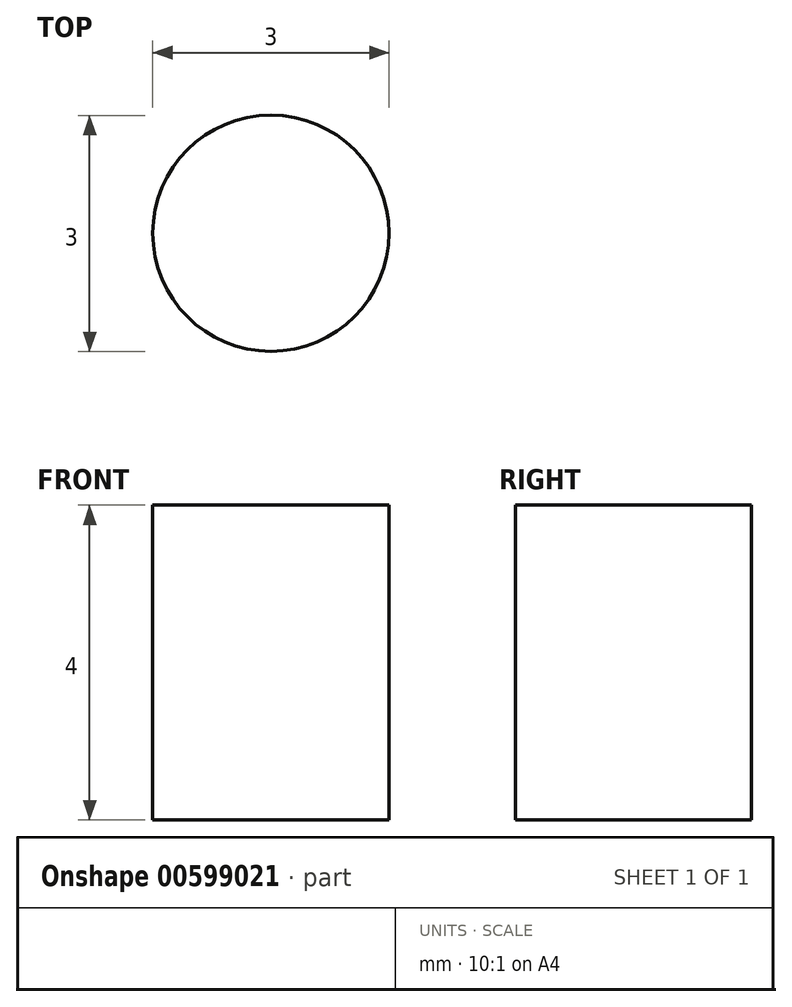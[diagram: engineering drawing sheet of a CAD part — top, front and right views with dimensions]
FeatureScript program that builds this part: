
annotation { "Feature Type Name" : "Feature", "Feature Type Description" : "" }
export const myFeature = defineFeature(function(context is Context, id is Id, definition is map)
    precondition{}
    {
        {
            var Q0;
            Q0=qCreatedBy(makeId("Top.planeOp"),FACE);
            var sketch = newSketch(context, id + "F0", { "sketchPlane" : qUnion([Q0])});
            skCircle(sketch, "E0", {"center": v(15.25, 15.25) * mm, "radius": 1.65 * mm});
            skPoint(sketch, "E1.middle", {"position": v(84.85, 84.85) * mm});
            skLineSegment(sketch, "E2.cCircle", {"start": v(56.25, 56.25) * mm, "end": v(56.25, 56.25) * mm});
            skLineSegment(sketch, "E3", {"start": v(84.85, 84.85) * mm, "end": v(0, 0) * mm, "construction": true});
            skLineSegment(sketch, "E4", {"start": v(14, 40) * mm, "end": v(11.06, 40) * mm});
            skCircle(sketch, "E5", {"center": v(84.85, 84.85) * mm, "radius": 63.5 * mm, "construction": true});
            skLineSegment(sketch, "E6", {"start": v(5.38, 24.29) * mm, "end": v(0, 24.29) * mm});
            skLineSegment(sketch, "E7", {"start": v(5.38, 24.29) * mm, "end": v(7.5, 26.4) * mm});
            skLineSegment(sketch, "E8", {"start": v(7.5, 26.4) * mm, "end": v(5.38, 28.53) * mm});
            skLineSegment(sketch, "E9", {"start": v(5.38, 28.53) * mm, "end": v(0, 28.53) * mm});
            skLineSegment(sketch, "E10", {"start": v(14, 40) * mm, "end": v(14, 0) * mm, "construction": true});
            skLineSegment(sketch, "E11.MirrorCS", {"start": v(-7.5, 26.4) * mm, "end": v(-5.38, 28.53) * mm});
            skLineSegment(sketch, "E12.MirrorCS", {"start": v(-5.38, 24.29) * mm, "end": v(-7.5, 26.4) * mm});
            skLineSegment(sketch, "E13.MirrorCS", {"start": v(-5.38, 28.53) * mm, "end": v(0, 28.53) * mm});
            skLineSegment(sketch, "E14.MirrorCS", {"start": v(-5.38, 24.29) * mm, "end": v(0, 24.29) * mm});
            skLineSegment(sketch, "E15.MirrorCS", {"start": v(20, 11.4) * mm, "end": v(17, 10) * mm});
            skLineSegment(sketch, "E16.MirrorCS", {"start": v(17, 10) * mm, "end": v(17, 0) * mm});
            skCircle(sketch, "E17", {"center": v(84.85, 84.85) * mm, "radius": 4.15 * mm});
            skLineSegment(sketch, "E18", {"start": v(20, 11.4) * mm, "end": v(78.33, 71.04) * mm});
            skLineSegment(sketch, "E19", {"start": v(14, 40) * mm, "end": v(20, 40) * mm, "construction": true});
            skLineSegment(sketch, "E20", {"start": v(20, 40) * mm, "end": v(20, 34) * mm, "construction": true});
            skLineSegment(sketch, "E21", {"start": v(20, 34) * mm, "end": v(14, 34) * mm, "construction": true});
            skCircle(sketch, "E22", {"center": v(17, 37) * mm, "radius": 1.65 * mm});
            skPoint(sketch, "E22.centerSnap0", {"position": v(20, 37) * mm});
            skPoint(sketch, "E22.centerSnap1", {"position": v(17, 40) * mm});
            skArc(sketch, "E23", {"start": v(83.25, 92.85) * mm, "mid": v(84.85, 91.25) * mm, "end": v(86.45, 92.85) * mm});
            skLineSegment(sketch, "E24.trimOffspring", {"start": v(86.45, 92.85) * mm, "end": v(86.45, 94.85) * mm});
            skLineSegment(sketch, "E25.trimOffspring", {"start": v(83.25, 92.85) * mm, "end": v(83.25, 94.35) * mm});
            skLineSegment(sketch, "E26.MirrorCS", {"start": v(83.25, 94.85) * mm, "end": v(83.25, 93.5) * mm});
            skLineSegment(sketch, "E27", {"start": v(14, 40) * mm, "end": v(20, 40) * mm});
            skLineSegment(sketch, "E28", {"start": v(20, 40) * mm, "end": v(80.19, 101.53) * mm});
            skCircle(sketch, "E29.cCircle", {"center": v(84.85, 84.85) * mm, "radius": 15 * mm, "construction": true});
            skLineSegment(sketch, "E29.0", {"start": v(68.07, 89.15) * mm, "end": v(80.19, 101.53) * mm});
            skLineSegment(sketch, "E29.1", {"start": v(80.19, 101.53) * mm, "end": v(96.96, 97.24) * mm});
            skLineSegment(sketch, "E29.2", {"start": v(96.96, 97.24) * mm, "end": v(101.63, 80.56) * mm});
            skLineSegment(sketch, "E29.3", {"start": v(101.63, 80.56) * mm, "end": v(89.52, 68.17) * mm});
            skLineSegment(sketch, "E29.4", {"start": v(89.52, 68.17) * mm, "end": v(72.74, 72.47) * mm});
            skLineSegment(sketch, "E29.5", {"start": v(72.74, 72.47) * mm, "end": v(68.07, 89.15) * mm});
            skPoint(sketch, "E29.0.midPoint", {"position": v(74.13, 95.34) * mm});
            skLineSegment(sketch, "E30", {"start": v(20, 11.4) * mm, "end": v(20, 34) * mm, "construction": true});
            skLineSegment(sketch, "E31", {"start": v(0, 37.6) * mm, "end": v(0, 28.53) * mm});
            skLineSegment(sketch, "E32", {"start": v(0, 24.29) * mm, "end": v(0, 0) * mm});
            skLineSegment(sketch, "E33", {"start": v(17, 0) * mm, "end": v(0, 0) * mm});
            skLineSegment(sketch, "E34", {"start": v(0, 37.6) * mm, "end": v(9, 37.6) * mm});
            skLineSegment(sketch, "E35", {"start": v(9, 37.6) * mm, "end": v(11.06, 40) * mm});
            skLineSegment(sketch, "E36", {"start": v(77.58, 84.85) * mm, "end": v(91.14, 84.85) * mm, "construction": true});
            skLineSegment(sketch, "E37", {"start": v(84.85, 90.4) * mm, "end": v(84.85, 78.23) * mm, "construction": true});
            skLineSegment(sketch, "E38", {"start": v(84.85, 92.85) * mm, "end": v(84.85, 94.85) * mm, "construction": true});
            skArc(sketch, "E39", {"start": v(86.45, 94.85) * mm, "mid": v(84.85, 96.45) * mm, "end": v(83.25, 94.85) * mm});
            skArc(sketch, "E40.MirrorCS", {"start": v(86.45, 92.85) * mm, "mid": v(84.85, 91.25) * mm, "end": v(83.25, 92.85) * mm});
            skLineSegment(sketch, "E41.MirrorCS", {"start": v(86.45, 92.85) * mm, "end": v(86.45, 94.35) * mm});
            skLineSegment(sketch, "E42.MirrorCS", {"start": v(83.25, 92.85) * mm, "end": v(83.25, 94.85) * mm});
            skLineSegment(sketch, "E43.MirrorCS", {"start": v(86.45, 94.85) * mm, "end": v(86.45, 93.5) * mm});
            skArc(sketch, "E44.MirrorCS", {"start": v(83.25, 94.85) * mm, "mid": v(84.85, 96.45) * mm, "end": v(86.45, 94.85) * mm});
            skLineSegment(sketch, "E45.MirrorCS", {"start": v(83.25, 94.85) * mm, "end": v(83.25, 95.2) * mm});
            skArc(sketch, "E46.MirrorCS", {"start": v(86.45, 76.85) * mm, "mid": v(84.85, 78.45) * mm, "end": v(83.25, 76.85) * mm});
            skLineSegment(sketch, "E47.MirrorCS", {"start": v(86.45, 76.85) * mm, "end": v(86.45, 75.35) * mm});
            skLineSegment(sketch, "E48.MirrorCS", {"start": v(86.45, 74.85) * mm, "end": v(86.45, 76.2) * mm});
            skArc(sketch, "E49.MirrorCS", {"start": v(83.25, 74.85) * mm, "mid": v(84.85, 73.25) * mm, "end": v(86.45, 74.85) * mm});
            skLineSegment(sketch, "E50.MirrorCS", {"start": v(83.25, 74.85) * mm, "end": v(83.25, 76.2) * mm});
            skLineSegment(sketch, "E51.MirrorCS", {"start": v(83.25, 76.85) * mm, "end": v(83.25, 74.85) * mm});
            skLineSegment(sketch, "E52", {"start": v(84.85, 84.85) * mm, "end": v(76.55, 93.16) * mm, "construction": true});
            skArc(sketch, "E53.MirrorCS", {"start": v(76.85, 83.25) * mm, "mid": v(78.45, 84.85) * mm, "end": v(76.85, 86.45) * mm});
            skLineSegment(sketch, "E54.MirrorCS", {"start": v(76.85, 83.25) * mm, "end": v(75.35, 83.25) * mm});
            skLineSegment(sketch, "E55.MirrorCS", {"start": v(74.85, 83.25) * mm, "end": v(76.2, 83.25) * mm});
            skArc(sketch, "E56.MirrorCS", {"start": v(74.85, 86.45) * mm, "mid": v(73.25, 84.85) * mm, "end": v(74.85, 83.25) * mm});
            skLineSegment(sketch, "E57.MirrorCS", {"start": v(74.85, 86.45) * mm, "end": v(76.2, 86.45) * mm});
            skLineSegment(sketch, "E58.MirrorCS", {"start": v(76.85, 86.45) * mm, "end": v(74.85, 86.45) * mm});
            skArc(sketch, "E59.MirrorCS", {"start": v(92.85, 83.25) * mm, "mid": v(91.25, 84.85) * mm, "end": v(92.85, 86.45) * mm});
            skLineSegment(sketch, "E60.MirrorCS", {"start": v(92.85, 86.45) * mm, "end": v(94.85, 86.45) * mm});
            skLineSegment(sketch, "E61.MirrorCS", {"start": v(94.85, 86.45) * mm, "end": v(93.5, 86.45) * mm});
            skArc(sketch, "E62.MirrorCS", {"start": v(94.85, 86.45) * mm, "mid": v(96.45, 84.85) * mm, "end": v(94.85, 83.25) * mm});
            skLineSegment(sketch, "E63.MirrorCS", {"start": v(94.85, 83.25) * mm, "end": v(93.5, 83.25) * mm});
            skLineSegment(sketch, "E64.MirrorCS", {"start": v(92.85, 83.25) * mm, "end": v(94.35, 83.25) * mm});
            skCircle(sketch, "E65.MirrorC", {"center": v(84.85, -84.85) * mm, "radius": 63.5 * mm, "construction": true});
            skPoint(sketch, "E66.orphan", {"position": v(74.5, 86.45) * mm});
            skPoint(sketch, "E67.orphan", {"position": v(95.2, 86.45) * mm});
            skPoint(sketch, "E68.orphan", {"position": v(83.25, 74.5) * mm});
            skPoint(sketch, "E69.start.orphan", {"position": v(86.45, 95.2) * mm});
            skSolve(sketch);
        }
        {
            var Q0;
            Q0=makeQuery(id+"F0.imprint","IMPRINT",FACE,{"disambiguationData":[TD([[makeQuery(id+"F0.imprint","IMPRINT",EDGE,{"derivedFrom":sQuery(id+"F0.wireOp",EDGE,"E0")}),-1.0]])]});
            var Q1;
            Q1=makeQuery(id+"F0.imprint","IMPRINT",FACE,{"disambiguationData":[TD([[makeQuery(id+"F0.imprint","IMPRINT",EDGE,{"derivedFrom":sQuery(id+"F0.wireOp",EDGE,"a8402e06-ee66-4db1-b534-accf88d6755370.MirrorCS")}),1.0]])]});
            var Q2;
            Q2=makeQuery(id+"F0.imprint","IMPRINT",FACE,{"disambiguationData":[TD([[makeQuery(id+"F0.imprint","IMPRINT",EDGE,{"derivedFrom":sQuery(id+"F0.wireOp",EDGE,"E17")}),-1.0]])]});
            extrude(context, id + "F1", {"entities" : qUnion([Q0, Q1, Q2]), "depth" : 4 * mm, "offsetDistance" : 25 * mm});
        }
        {
            var Q0;
            Q0=makeQuery(id+"F1.opExtrude","SWEPT_EDGE",EDGE,{"disambiguationData":[OSD([sQuery(id+"F0.wireOp",EDGE,"jGvzkioU-qR6A-EtLG-xQrp-rLiX74bcyy6I"),sQuery(id+"F0.wireOp",EDGE,"c73e3937-3783-43b0-b012-681b517a04ab3.MirrorCS")])]});
            var Q1;
            Q1=makeQuery(id+"F1.opExtrude","SWEPT_EDGE",EDGE,{"disambiguationData":[OSD([sQuery(id+"F0.wireOp",EDGE,"c73e3937-3783-43b0-b012-681b517a04ab3.MirrorCS"),sQuery(id+"F0.wireOp",EDGE,"c73e3937-3783-43b0-b012-681b517a04ab4.MirrorCS")])]});
            var Q2;
            Q2=makeQuery(id+"F1.opExtrude","SWEPT_EDGE",EDGE,{"disambiguationData":[OSD([sQuery(id+"F0.wireOp",EDGE,"c73e3937-3783-43b0-b012-681b517a04ab2.MirrorCS"),sQuery(id+"F0.wireOp",EDGE,"c73e3937-3783-43b0-b012-681b517a04ab4.MirrorCS")])]});
            var Q3;
            Q3=makeQuery(id+"F1.opExtrude","SWEPT_EDGE",EDGE,{"disambiguationData":[OSD([sQuery(id+"F0.wireOp",EDGE,"c73e3937-3783-43b0-b012-681b517a04ab1.MirrorCS"),sQuery(id+"F0.wireOp",EDGE,"c73e3937-3783-43b0-b012-681b517a04ab2.MirrorCS")])]});
            var Q4;
            Q4=makeQuery(id+"F1.opExtrude","SWEPT_EDGE",EDGE,{"disambiguationData":[OSD([sQuery(id+"F0.wireOp",EDGE,"c73e3937-3783-43b0-b012-681b517a04ab0.MirrorCS"),sQuery(id+"F0.wireOp",EDGE,"c73e3937-3783-43b0-b012-681b517a04ab1.MirrorCS")])]});
            var Q5;
            {var subQ0=sQuery(id+"F0.wireOp",EDGE,"E18");Q5=qUnion([makeQuery(id+"F1.opExtrude","SWEPT_EDGE",EDGE,{"disambiguationData":[OSD([sQuery(id+"F0.wireOp",EDGE,"E15.MirrorCS"),subQ0])]}),makeQuery(id+"F1.opExtrude","SWEPT_EDGE",EDGE,{"disambiguationData":[OSD([subQ0,sQuery(id+"F0.wireOp",EDGE,"E29.4")])]})]);}
            var Q6;
            {var subQ0=sQuery(id+"F0.wireOp",EDGE,"E18");Q6=qUnion([makeQuery(id+"F1.opExtrude","SWEPT_EDGE",EDGE,{"disambiguationData":[OSD([sQuery(id+"F0.wireOp",EDGE,"E15.MirrorCS"),subQ0])]}),makeQuery(id+"F1.opExtrude","SWEPT_EDGE",EDGE,{"disambiguationData":[OSD([subQ0,sQuery(id+"F0.wireOp",EDGE,"E29.4")])]})]);}
            var Q7;
            {var subQ0=sQuery(id+"F0.wireOp",EDGE,"E15.MirrorCS");Q7=qUnion([makeQuery(id+"F1.opExtrude","SWEPT_EDGE",EDGE,{"disambiguationData":[OSD([subQ0,sQuery(id+"F0.wireOp",EDGE,"E18")])]}),makeQuery(id+"F1.opExtrude","SWEPT_EDGE",EDGE,{"disambiguationData":[OSD([subQ0,sQuery(id+"F0.wireOp",EDGE,"E16.MirrorCS")])]})]);}
            var Q8;
            Q8=makeQuery(id+"F1.opExtrude","SWEPT_EDGE",EDGE,{"disambiguationData":[OSD([sQuery(id+"F0.wireOp",EDGE,"E15.MirrorCS"),sQuery(id+"F0.wireOp",EDGE,"E16.MirrorCS")])]});
            var Q9;
            Q9=makeQuery(id+"F1.opExtrude","SWEPT_EDGE",EDGE,{"disambiguationData":[OSD([sQuery(id+"F0.wireOp",EDGE,"ATg7OfvZ-YIOK-q6A6-GKlu-KA3SPvuErL9v"),sQuery(id+"F0.wireOp",EDGE,"gxQ5UFMt-oJty-NrjN-UH2Y-Adpejihou7FO")])]});
            var Q10;
            Q10=makeQuery(id+"F1.opExtrude","SWEPT_EDGE",EDGE,{"disambiguationData":[OSD([sQuery(id+"F0.wireOp",EDGE,"d21186f0-3676-4457-b274-e7f54dffb324103.MirrorCS"),sQuery(id+"F0.wireOp",EDGE,"ATg7OfvZ-YIOK-q6A6-GKlu-KA3SPvuErL9v")])]});
            var Q11;
            Q11=makeQuery(id+"F1.opExtrude","SWEPT_EDGE",EDGE,{"disambiguationData":[OSD([sQuery(id+"F0.wireOp",EDGE,"d21186f0-3676-4457-b274-e7f54dffb324103.MirrorCS"),sQuery(id+"F0.wireOp",EDGE,"6f5b9e03-edb7-4fd9-bd29-0bbe677f39fa0.MirrorCS")])]});
            var Q12;
            Q12=makeQuery(id+"F1.opExtrude","SWEPT_EDGE",EDGE,{"disambiguationData":[OSD([sQuery(id+"F0.wireOp",EDGE,"4ac17b15-1a57-428c-943a-6c9f986613ac.2"),sQuery(id+"F0.wireOp",EDGE,"6f5b9e03-edb7-4fd9-bd29-0bbe677f39fa0.MirrorCS")])]});
            var Q13;
            Q13=makeQuery(id+"F1.opExtrude","SWEPT_EDGE",EDGE,{"disambiguationData":[OSD([sQuery(id+"F0.wireOp",EDGE,"4ac17b15-1a57-428c-943a-6c9f986613ac.2"),sQuery(id+"F0.wireOp",EDGE,"4ac17b15-1a57-428c-943a-6c9f986613ac.3")])]});
            var Q14;
            Q14=makeQuery(id+"F1.opExtrude","SWEPT_EDGE",EDGE,{"disambiguationData":[OSD([sQuery(id+"F0.wireOp",EDGE,"4ac17b15-1a57-428c-943a-6c9f986613ac.3"),sQuery(id+"F0.wireOp",EDGE,"4ac17b15-1a57-428c-943a-6c9f986613ac.4")])]});
            var Q15;
            Q15=makeQuery(id+"F1.opExtrude","SWEPT_EDGE",EDGE,{"disambiguationData":[OSD([sQuery(id+"F0.wireOp",EDGE,"4ac17b15-1a57-428c-943a-6c9f986613ac.4"),sQuery(id+"F0.wireOp",EDGE,"4ac17b15-1a57-428c-943a-6c9f986613ac.5")])]});
            var Q16;
            Q16=makeQuery(id+"F1.opExtrude","SWEPT_EDGE",EDGE,{"disambiguationData":[OSD([sQuery(id+"F0.wireOp",EDGE,"4ac17b15-1a57-428c-943a-6c9f986613ac.0"),sQuery(id+"F0.wireOp",EDGE,"4ac17b15-1a57-428c-943a-6c9f986613ac.5")])]});
            var Q17;
            Q17=makeQuery(id+"F1.opExtrude","SWEPT_EDGE",EDGE,{"disambiguationData":[OSD([sQuery(id+"F0.wireOp",EDGE,"d21186f0-3676-4457-b274-e7f54dffb32479.MirrorCS"),sQuery(id+"F0.wireOp",EDGE,"4ac17b15-1a57-428c-943a-6c9f986613ac.0")])]});
            var Q18;
            Q18=makeQuery(id+"F1.opExtrude","SWEPT_EDGE",EDGE,{"disambiguationData":[OSD([sQuery(id+"F0.wireOp",EDGE,"d21186f0-3676-4457-b274-e7f54dffb32468.MirrorCS"),sQuery(id+"F0.wireOp",EDGE,"d21186f0-3676-4457-b274-e7f54dffb32479.MirrorCS")])]});
            var Q19;
            Q19=makeQuery(id+"F1.opExtrude","SWEPT_EDGE",EDGE,{"disambiguationData":[OSD([sQuery(id+"F0.wireOp",EDGE,"d21186f0-3676-4457-b274-e7f54dffb32481.MirrorCS"),sQuery(id+"F0.wireOp",EDGE,"d21186f0-3676-4457-b274-e7f54dffb324119.MirrorCS")])]});
            var Q20;
            Q20=makeQuery(id+"F1.opExtrude","SWEPT_EDGE",EDGE,{"disambiguationData":[OSD([sQuery(id+"F0.wireOp",EDGE,"d21186f0-3676-4457-b274-e7f54dffb324119.MirrorCS"),sQuery(id+"F0.wireOp",EDGE,"76a94fc9-4153-4bcc-bea7-408b991e1d1c3.MirrorCS")])]});
            var Q21;
            Q21=makeQuery(id+"F1.opExtrude","SWEPT_EDGE",EDGE,{"disambiguationData":[OSD([sQuery(id+"F0.wireOp",EDGE,"76a94fc9-4153-4bcc-bea7-408b991e1d1c3.MirrorCS"),sQuery(id+"F0.wireOp",EDGE,"76a94fc9-4153-4bcc-bea7-408b991e1d1c4.MirrorCS")])]});
            var Q22;
            Q22=makeQuery(id+"F1.opExtrude","SWEPT_EDGE",EDGE,{"disambiguationData":[OSD([sQuery(id+"F0.wireOp",EDGE,"76a94fc9-4153-4bcc-bea7-408b991e1d1c2.MirrorCS"),sQuery(id+"F0.wireOp",EDGE,"76a94fc9-4153-4bcc-bea7-408b991e1d1c4.MirrorCS")])]});
            var Q23;
            Q23=makeQuery(id+"F1.opExtrude","SWEPT_EDGE",EDGE,{"disambiguationData":[OSD([sQuery(id+"F0.wireOp",EDGE,"76a94fc9-4153-4bcc-bea7-408b991e1d1c1.MirrorCS"),sQuery(id+"F0.wireOp",EDGE,"76a94fc9-4153-4bcc-bea7-408b991e1d1c2.MirrorCS")])]});
            var Q24;
            Q24=makeQuery(id+"F1.opExtrude","SWEPT_EDGE",EDGE,{"disambiguationData":[OSD([sQuery(id+"F0.wireOp",EDGE,"76a94fc9-4153-4bcc-bea7-408b991e1d1c0.MirrorCS"),sQuery(id+"F0.wireOp",EDGE,"76a94fc9-4153-4bcc-bea7-408b991e1d1c1.MirrorCS")])]});
            var Q25;
            Q25=makeQuery(id+"F1.opExtrude","SWEPT_EDGE",EDGE,{"disambiguationData":[OSD([sQuery(id+"F0.wireOp",EDGE,"76a94fc9-4153-4bcc-bea7-408b991e1d1c0.MirrorCS"),sQuery(id+"F0.wireOp",EDGE,"6d48d0eb-1f29-4900-b3be-e3536e2e83870.MirrorCS")])]});
            var Q26;
            Q26=makeQuery(id+"F1.opExtrude","SWEPT_EDGE",EDGE,{"disambiguationData":[OSD([sQuery(id+"F0.wireOp",EDGE,"5b215c89-2612-4b35-8ec4-2e2aefe904ed2.MirrorCS"),sQuery(id+"F0.wireOp",EDGE,"6d48d0eb-1f29-4900-b3be-e3536e2e83870.MirrorCS")])]});
            var Q27;
            Q27=makeQuery(id+"F1.opExtrude","SWEPT_EDGE",EDGE,{"disambiguationData":[OSD([sQuery(id+"F0.wireOp",EDGE,"5b215c89-2612-4b35-8ec4-2e2aefe904ed2.MirrorCS"),sQuery(id+"F0.wireOp",EDGE,"5b215c89-2612-4b35-8ec4-2e2aefe904ed3.MirrorCS")])]});
            var Q28;
            Q28=makeQuery(id+"F1.opExtrude","SWEPT_EDGE",EDGE,{"disambiguationData":[OSD([sQuery(id+"F0.wireOp",EDGE,"5b215c89-2612-4b35-8ec4-2e2aefe904ed3.MirrorCS"),sQuery(id+"F0.wireOp",EDGE,"5b215c89-2612-4b35-8ec4-2e2aefe904ed4.MirrorCS")])]});
            var Q29;
            Q29=makeQuery(id+"F1.opExtrude","SWEPT_EDGE",EDGE,{"disambiguationData":[OSD([sQuery(id+"F0.wireOp",EDGE,"5b215c89-2612-4b35-8ec4-2e2aefe904ed1.MirrorCS"),sQuery(id+"F0.wireOp",EDGE,"5b215c89-2612-4b35-8ec4-2e2aefe904ed5.MirrorCS")])]});
            var Q30;
            Q30=makeQuery(id+"F1.opExtrude","SWEPT_EDGE",EDGE,{"disambiguationData":[OSD([sQuery(id+"F0.wireOp",EDGE,"5b215c89-2612-4b35-8ec4-2e2aefe904ed0.MirrorCS"),sQuery(id+"F0.wireOp",EDGE,"5b215c89-2612-4b35-8ec4-2e2aefe904ed5.MirrorCS")])]});
            var Q31;
            Q31=makeQuery(id+"F1.opExtrude","SWEPT_EDGE",EDGE,{"disambiguationData":[OSD([sQuery(id+"F0.wireOp",EDGE,"5b215c89-2612-4b35-8ec4-2e2aefe904ed0.MirrorCS"),sQuery(id+"F0.wireOp",EDGE,"7c8dc105-e33c-482c-8640-72da622ad4630.MirrorCS")])]});
            var Q32;
            Q32=makeQuery(id+"F1.opExtrude","SWEPT_EDGE",EDGE,{"disambiguationData":[OSD([sQuery(id+"F0.wireOp",EDGE,"7e529d84-9969-4e5d-990a-ac009d21d78a0.MirrorCS"),sQuery(id+"F0.wireOp",EDGE,"7c8dc105-e33c-482c-8640-72da622ad4630.MirrorCS")])]});
            var Q33;
            Q33=makeQuery(id+"F1.opExtrude","SWEPT_EDGE",EDGE,{"disambiguationData":[OSD([sQuery(id+"F0.wireOp",EDGE,"7e529d84-9969-4e5d-990a-ac009d21d78a0.MirrorCS"),sQuery(id+"F0.wireOp",EDGE,"7e529d84-9969-4e5d-990a-ac009d21d78a1.MirrorCS")])]});
            var Q34;
            Q34=makeQuery(id+"F1.opExtrude","SWEPT_EDGE",EDGE,{"disambiguationData":[OSD([sQuery(id+"F0.wireOp",EDGE,"7e529d84-9969-4e5d-990a-ac009d21d78a1.MirrorCS"),sQuery(id+"F0.wireOp",EDGE,"7e529d84-9969-4e5d-990a-ac009d21d78a2.MirrorCS")])]});
            var Q35;
            Q35=makeQuery(id+"F1.opExtrude","SWEPT_EDGE",EDGE,{"disambiguationData":[OSD([sQuery(id+"F0.wireOp",EDGE,"7e529d84-9969-4e5d-990a-ac009d21d78a2.MirrorCS"),sQuery(id+"F0.wireOp",EDGE,"7e529d84-9969-4e5d-990a-ac009d21d78a4.MirrorCS")])]});
            var Q36;
            Q36=makeQuery(id+"F1.opExtrude","SWEPT_EDGE",EDGE,{"disambiguationData":[OSD([sQuery(id+"F0.wireOp",EDGE,"7e529d84-9969-4e5d-990a-ac009d21d78a3.MirrorCS"),sQuery(id+"F0.wireOp",EDGE,"7e529d84-9969-4e5d-990a-ac009d21d78a4.MirrorCS")])]});
            var Q37;
            Q37=makeQuery(id+"F1.opExtrude","SWEPT_EDGE",EDGE,{"disambiguationData":[OSD([sQuery(id+"F0.wireOp",EDGE,"2c355935-e90a-4b73-921b-e13c2be87c5e59.MirrorCS"),sQuery(id+"F0.wireOp",EDGE,"7e529d84-9969-4e5d-990a-ac009d21d78a3.MirrorCS")])]});
            var Q38;
            Q38=makeQuery(id+"F1.opExtrude","SWEPT_EDGE",EDGE,{"disambiguationData":[OSD([sQuery(id+"F0.wireOp",EDGE,"2c355935-e90a-4b73-921b-e13c2be87c5e50.MirrorCS"),sQuery(id+"F0.wireOp",EDGE,"2c355935-e90a-4b73-921b-e13c2be87c5e59.MirrorCS")])]});
            var Q39;
            Q39=makeQuery(id+"F1.opExtrude","SWEPT_EDGE",EDGE,{"disambiguationData":[OSD([sQuery(id+"F0.wireOp",EDGE,"E29.3"),sQuery(id+"F0.wireOp",EDGE,"E29.4")])]});
            var Q40;
            Q40=makeQuery(id+"F1.opExtrude","SWEPT_EDGE",EDGE,{"disambiguationData":[OSD([sQuery(id+"F0.wireOp",EDGE,"E29.2"),sQuery(id+"F0.wireOp",EDGE,"E29.3")])]});
            var Q41;
            Q41=makeQuery(id+"F1.opExtrude","SWEPT_EDGE",EDGE,{"disambiguationData":[OSD([sQuery(id+"F0.wireOp",EDGE,"E29.1"),sQuery(id+"F0.wireOp",EDGE,"E29.2")])]});
            var Q42;
            Q42=makeQuery(id+"F1.opExtrude","SWEPT_EDGE",EDGE,{"disambiguationData":[OSD([sQuery(id+"F0.wireOp",EDGE,"E28"),sQuery(id+"F0.wireOp",EDGE,"E29.1")])]});
            var Q43;
            Q43=makeQuery(id+"F1.opExtrude","SWEPT_EDGE",EDGE,{"disambiguationData":[OSD([sQuery(id+"F0.wireOp",EDGE,"E27"),sQuery(id+"F0.wireOp",EDGE,"E28")])]});
            var Q44;
            Q44=makeQuery(id+"F1.opExtrude","SWEPT_EDGE",EDGE,{"disambiguationData":[OSD([sQuery(id+"F0.wireOp",EDGE,"E4"),sQuery(id+"F0.wireOp",EDGE,"E35")])]});
            var Q45;
            Q45=makeQuery(id+"F1.opExtrude","SWEPT_EDGE",EDGE,{"disambiguationData":[OSD([sQuery(id+"F0.wireOp",EDGE,"E34"),sQuery(id+"F0.wireOp",EDGE,"E35")])]});
            fillet(context, id + "F2", {"entities" : qUnion([Q0, Q1, Q2, Q3, Q4, Q5, Q6, Q7, Q8, Q9, Q10, Q11, Q12, Q13, Q14, Q15, Q16, Q17, Q18, Q19, Q20, Q21, Q22, Q23, Q24, Q25, Q26, Q27, Q28, Q29, Q30, Q31, Q32, Q33, Q34, Q35, Q36, Q37, Q38, Q39, Q40, Q41, Q42, Q43, Q44, Q45]), "radius" : 3 * mm, "tangentPropagation" : true, "allowEdgeOverflow" : false});
        }
        {
            var Q0;
            Q0=makeQuery(id+"F1.opExtrude","SWEPT_BODY",BODY,{"disambiguationData":[OSD([sQuery(id+"F0.wireOp",EDGE,"E0"),sQuery(id+"F0.wireOp",EDGE,"E4"),sQuery(id+"F0.wireOp",EDGE,"E6"),sQuery(id+"F0.wireOp",EDGE,"E7"),sQuery(id+"F0.wireOp",EDGE,"E8"),sQuery(id+"F0.wireOp",EDGE,"E9"),sQuery(id+"F0.wireOp",EDGE,"E15.MirrorCS"),sQuery(id+"F0.wireOp",EDGE,"E16.MirrorCS"),sQuery(id+"F0.wireOp",EDGE,"E17"),sQuery(id+"F0.wireOp",EDGE,"E18"),sQuery(id+"F0.wireOp",EDGE,"E22"),sQuery(id+"F0.wireOp",EDGE,"E23"),sQuery(id+"F0.wireOp",EDGE,"E24.trimOffspring"),sQuery(id+"F0.wireOp",EDGE,"E25.trimOffspring"),sQuery(id+"F0.wireOp",EDGE,"E26.MirrorCS"),sQuery(id+"F0.wireOp",EDGE,"E27"),sQuery(id+"F0.wireOp",EDGE,"E28"),sQuery(id+"F0.wireOp",EDGE,"E29.1"),sQuery(id+"F0.wireOp",EDGE,"E29.2"),sQuery(id+"F0.wireOp",EDGE,"E29.3"),sQuery(id+"F0.wireOp",EDGE,"E29.4"),sQuery(id+"F0.wireOp",EDGE,"E31"),sQuery(id+"F0.wireOp",EDGE,"E32"),sQuery(id+"F0.wireOp",EDGE,"E33"),sQuery(id+"F0.wireOp",EDGE,"E34"),sQuery(id+"F0.wireOp",EDGE,"E35"),sQuery(id+"F0.wireOp",EDGE,"E39"),sQuery(id+"F0.wireOp",EDGE,"E46.MirrorCS"),sQuery(id+"F0.wireOp",EDGE,"E47.MirrorCS"),sQuery(id+"F0.wireOp",EDGE,"E48.MirrorCS"),sQuery(id+"F0.wireOp",EDGE,"E49.MirrorCS"),sQuery(id+"F0.wireOp",EDGE,"E50.MirrorCS"),sQuery(id+"F0.wireOp",EDGE,"E51.MirrorCS"),sQuery(id+"F0.wireOp",EDGE,"E53.MirrorCS"),sQuery(id+"F0.wireOp",EDGE,"E54.MirrorCS"),sQuery(id+"F0.wireOp",EDGE,"E55.MirrorCS"),sQuery(id+"F0.wireOp",EDGE,"E56.MirrorCS"),sQuery(id+"F0.wireOp",EDGE,"E57.MirrorCS"),sQuery(id+"F0.wireOp",EDGE,"E58.MirrorCS"),sQuery(id+"F0.wireOp",EDGE,"E59.MirrorCS"),sQuery(id+"F0.wireOp",EDGE,"E60.MirrorCS"),sQuery(id+"F0.wireOp",EDGE,"E62.MirrorCS"),sQuery(id+"F0.wireOp",EDGE,"E63.MirrorCS"),sQuery(id+"F0.wireOp",EDGE,"E64.MirrorCS")])]});
            var Q1;
            Q1=qCreatedBy(makeId("Right.planeOp"),FACE);
            mirror(context, id + "F3", {"operationType" : NewBodyOperationType.ADD, "entities" : qUnion([Q0]), "mirrorPlane" : qUnion([Q1])});
        }
        {
            var Q0;
            Q0=makeQuery(id+"F1.opExtrude","SWEPT_BODY",BODY,{"disambiguationData":[OSD([sQuery(id+"F0.wireOp",EDGE,"E0"),sQuery(id+"F0.wireOp",EDGE,"E4"),sQuery(id+"F0.wireOp",EDGE,"E6"),sQuery(id+"F0.wireOp",EDGE,"E7"),sQuery(id+"F0.wireOp",EDGE,"E8"),sQuery(id+"F0.wireOp",EDGE,"E9"),sQuery(id+"F0.wireOp",EDGE,"E15.MirrorCS"),sQuery(id+"F0.wireOp",EDGE,"E16.MirrorCS"),sQuery(id+"F0.wireOp",EDGE,"E17"),sQuery(id+"F0.wireOp",EDGE,"E18"),sQuery(id+"F0.wireOp",EDGE,"E22"),sQuery(id+"F0.wireOp",EDGE,"E23"),sQuery(id+"F0.wireOp",EDGE,"E24.trimOffspring"),sQuery(id+"F0.wireOp",EDGE,"E25.trimOffspring"),sQuery(id+"F0.wireOp",EDGE,"E26.MirrorCS"),sQuery(id+"F0.wireOp",EDGE,"E27"),sQuery(id+"F0.wireOp",EDGE,"E28"),sQuery(id+"F0.wireOp",EDGE,"E29.1"),sQuery(id+"F0.wireOp",EDGE,"E29.2"),sQuery(id+"F0.wireOp",EDGE,"E29.3"),sQuery(id+"F0.wireOp",EDGE,"E29.4"),sQuery(id+"F0.wireOp",EDGE,"E31"),sQuery(id+"F0.wireOp",EDGE,"E32"),sQuery(id+"F0.wireOp",EDGE,"E33"),sQuery(id+"F0.wireOp",EDGE,"E34"),sQuery(id+"F0.wireOp",EDGE,"E35"),sQuery(id+"F0.wireOp",EDGE,"E39"),sQuery(id+"F0.wireOp",EDGE,"E46.MirrorCS"),sQuery(id+"F0.wireOp",EDGE,"E47.MirrorCS"),sQuery(id+"F0.wireOp",EDGE,"E48.MirrorCS"),sQuery(id+"F0.wireOp",EDGE,"E49.MirrorCS"),sQuery(id+"F0.wireOp",EDGE,"E50.MirrorCS"),sQuery(id+"F0.wireOp",EDGE,"E51.MirrorCS"),sQuery(id+"F0.wireOp",EDGE,"E53.MirrorCS"),sQuery(id+"F0.wireOp",EDGE,"E54.MirrorCS"),sQuery(id+"F0.wireOp",EDGE,"E55.MirrorCS"),sQuery(id+"F0.wireOp",EDGE,"E56.MirrorCS"),sQuery(id+"F0.wireOp",EDGE,"E57.MirrorCS"),sQuery(id+"F0.wireOp",EDGE,"E58.MirrorCS"),sQuery(id+"F0.wireOp",EDGE,"E59.MirrorCS"),sQuery(id+"F0.wireOp",EDGE,"E60.MirrorCS"),sQuery(id+"F0.wireOp",EDGE,"E62.MirrorCS"),sQuery(id+"F0.wireOp",EDGE,"E63.MirrorCS"),sQuery(id+"F0.wireOp",EDGE,"E64.MirrorCS")])]});
            var Q1;
            Q1=qCreatedBy(makeId("Front.planeOp"),FACE);
            mirror(context, id + "F4", {"operationType" : NewBodyOperationType.ADD, "entities" : qUnion([Q0]), "mirrorPlane" : qUnion([Q1])});
        }
        {
            var Q0;
            {var subQ0=makeQuery(id+"F1.opExtrude","CAP_FACE",FACE,{"disambiguationData":[OSD([sQuery(id+"F0.wireOp",EDGE,"E0"),sQuery(id+"F0.wireOp",EDGE,"E4"),sQuery(id+"F0.wireOp",EDGE,"E6"),sQuery(id+"F0.wireOp",EDGE,"E7"),sQuery(id+"F0.wireOp",EDGE,"E8"),sQuery(id+"F0.wireOp",EDGE,"E9"),sQuery(id+"F0.wireOp",EDGE,"E15.MirrorCS"),sQuery(id+"F0.wireOp",EDGE,"E16.MirrorCS"),sQuery(id+"F0.wireOp",EDGE,"E17"),sQuery(id+"F0.wireOp",EDGE,"E18"),sQuery(id+"F0.wireOp",EDGE,"E22"),sQuery(id+"F0.wireOp",EDGE,"E23"),sQuery(id+"F0.wireOp",EDGE,"E24.trimOffspring"),sQuery(id+"F0.wireOp",EDGE,"E25.trimOffspring"),sQuery(id+"F0.wireOp",EDGE,"E26.MirrorCS"),sQuery(id+"F0.wireOp",EDGE,"E27"),sQuery(id+"F0.wireOp",EDGE,"E28"),sQuery(id+"F0.wireOp",EDGE,"E29.1"),sQuery(id+"F0.wireOp",EDGE,"E29.2"),sQuery(id+"F0.wireOp",EDGE,"E29.3"),sQuery(id+"F0.wireOp",EDGE,"E29.4"),sQuery(id+"F0.wireOp",EDGE,"E31"),sQuery(id+"F0.wireOp",EDGE,"E32"),sQuery(id+"F0.wireOp",EDGE,"E33"),sQuery(id+"F0.wireOp",EDGE,"E34"),sQuery(id+"F0.wireOp",EDGE,"E35"),sQuery(id+"F0.wireOp",EDGE,"E39"),sQuery(id+"F0.wireOp",EDGE,"E46.MirrorCS"),sQuery(id+"F0.wireOp",EDGE,"E47.MirrorCS"),sQuery(id+"F0.wireOp",EDGE,"E48.MirrorCS"),sQuery(id+"F0.wireOp",EDGE,"E49.MirrorCS"),sQuery(id+"F0.wireOp",EDGE,"E50.MirrorCS"),sQuery(id+"F0.wireOp",EDGE,"E51.MirrorCS"),sQuery(id+"F0.wireOp",EDGE,"E53.MirrorCS"),sQuery(id+"F0.wireOp",EDGE,"E54.MirrorCS"),sQuery(id+"F0.wireOp",EDGE,"E55.MirrorCS"),sQuery(id+"F0.wireOp",EDGE,"E56.MirrorCS"),sQuery(id+"F0.wireOp",EDGE,"E57.MirrorCS"),sQuery(id+"F0.wireOp",EDGE,"E58.MirrorCS"),sQuery(id+"F0.wireOp",EDGE,"E59.MirrorCS"),sQuery(id+"F0.wireOp",EDGE,"E60.MirrorCS"),sQuery(id+"F0.wireOp",EDGE,"E62.MirrorCS"),sQuery(id+"F0.wireOp",EDGE,"E63.MirrorCS"),sQuery(id+"F0.wireOp",EDGE,"E64.MirrorCS")])],"isStart":false});var subQ1=makeQuery(id+"F3.boolean.opBoolean","MERGE",FACE,{"derivedFrom":[subQ0,makeQuery(id+"F3.opPattern","COPY",FACE,{"derivedFrom":subQ0,"instanceName":"1"})]});Q0=makeQuery(id+"F4.boolean.opBoolean","MERGE",FACE,{"derivedFrom":[subQ1,makeQuery(id+"F4.opPattern","COPY",FACE,{"derivedFrom":subQ1,"instanceName":"1"})]});}
            var sketch = newSketch(context, id + "F5", { "sketchPlane" : qUnion([Q0])});
            skLineSegment(sketch, "E70", {"start": v(0, 0) * mm, "end": v(0, -28.53) * mm, "construction": true});
            skLineSegment(sketch, "E71", {"start": v(0, -28.53) * mm, "end": v(0, -37.6) * mm, "construction": true});
            skLineSegment(sketch, "E72", {"start": v(0, -33.07) * mm, "end": v(7.5, -33.07) * mm, "construction": true});
            skCircle(sketch, "E73", {"center": v(7.5, -33.07) * mm, "radius": 1.5 * mm});
            skCircle(sketch, "E74.MirrorC", {"center": v(-7.5, -33.07) * mm, "radius": 1.5 * mm});
            skSolve(sketch);
        }
        {
            var Q0;
            Q0=makeQuery(id+"F5.imprint","IMPRINT",FACE,{"disambiguationData":[TD([[makeQuery(id+"F5.imprint","IMPRINT",EDGE,{"derivedFrom":sQuery(id+"F5.wireOp",EDGE,"E74.MirrorC")}),-1.0]])]});
            var Q1;
            Q1=makeQuery(id+"F5.imprint","IMPRINT",FACE,{"disambiguationData":[TD([[makeQuery(id+"F5.imprint","IMPRINT",EDGE,{"derivedFrom":sQuery(id+"F5.wireOp",EDGE,"E73")}),1.0]])]});
            extrude(context, id + "F6", {"entities" : qUnion([Q0, Q1]), "operationType" : NewBodyOperationType.REMOVE, "endBound" : BoundingType.SYMMETRIC, "oppositeDirection" : true, "depth" : 87 * mm, "offsetDistance" : 25 * mm});
        }
    });
